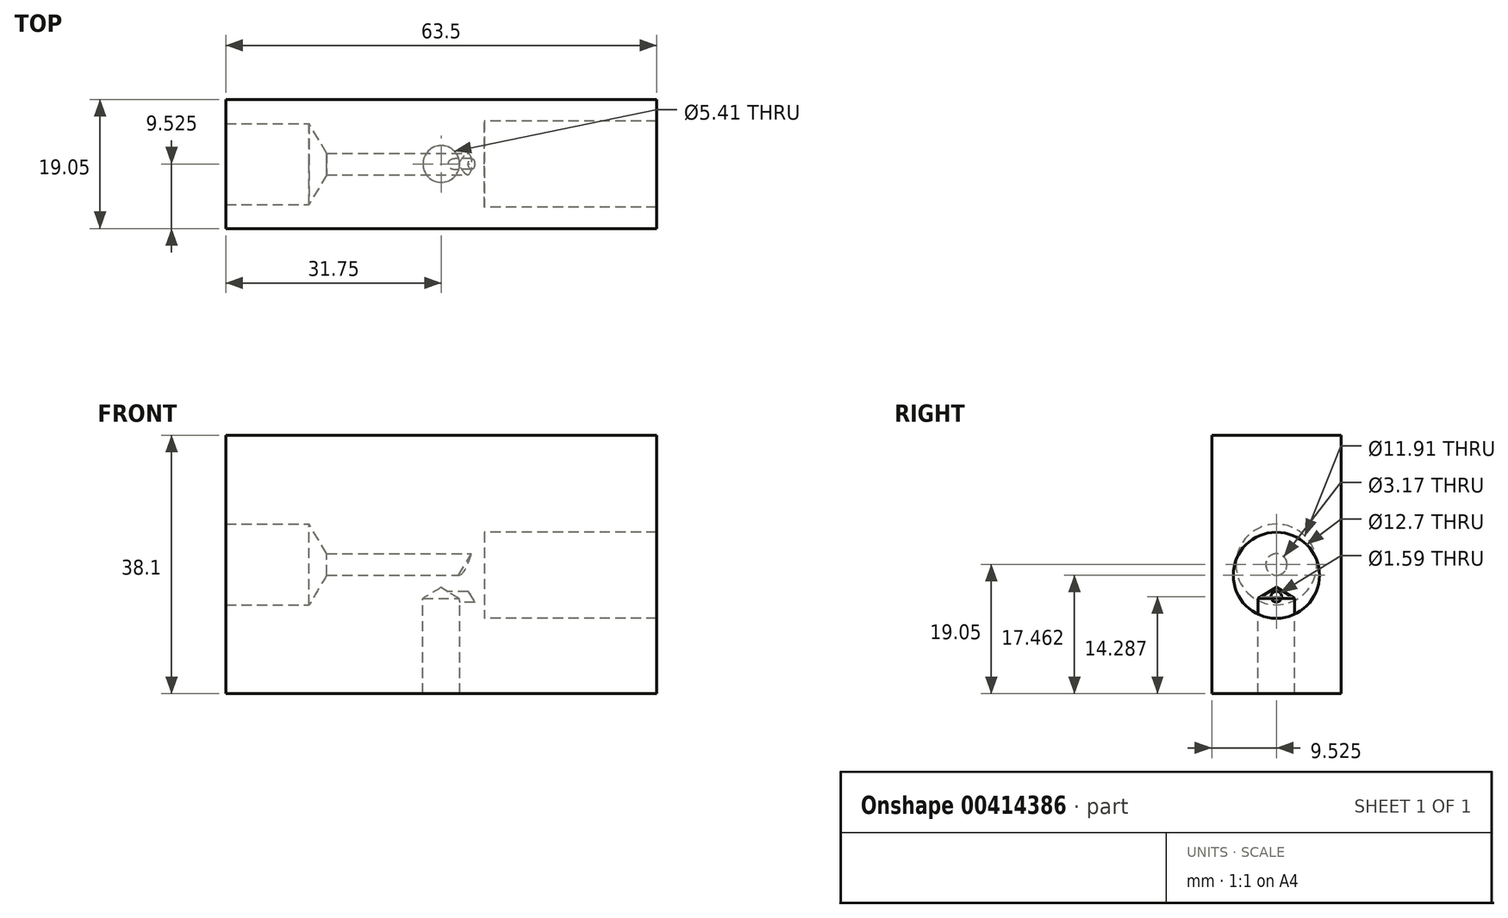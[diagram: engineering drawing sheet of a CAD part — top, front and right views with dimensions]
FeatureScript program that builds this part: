
annotation { "Feature Type Name" : "Feature", "Feature Type Description" : "" }
export const myFeature = defineFeature(function(context is Context, id is Id, definition is map)
    precondition{}
    {
        {
            var Q0;
            Q0=qCreatedBy(makeId("Front.planeOp"),FACE);
            var sketch = newSketch(context, id + "F0", { "sketchPlane" : qUnion([Q0])});
            skLineSegment(sketch, "E0.bottom", {"start": v(0, 0) * mm, "end": v(-63.5, 0) * mm});
            skLineSegment(sketch, "E0.top", {"start": v(0, 38.1) * mm, "end": v(-63.5, 38.1) * mm});
            skLineSegment(sketch, "E0.left", {"start": v(0, 0) * mm, "end": v(0, 38.1) * mm});
            skLineSegment(sketch, "E0.right", {"start": v(-63.5, 0) * mm, "end": v(-63.5, 38.1) * mm});
            skSolve(sketch);
        }
        {
            var Q0;
            Q0=makeQuery(id+"F0.imprint","IMPRINT",FACE,{"disambiguationData":[TD([[makeQuery(id+"F0.imprint","IMPRINT",EDGE,{"derivedFrom":sQuery(id+"F0.wireOp",EDGE,"E0.bottom")}),-1.0]])]});
            extrude(context, id + "F1", {"entities" : qUnion([Q0]), "depth" : 19.05 * mm, "offsetDistance" : 25.4 * mm});
        }
        {
            var Q0;
            Q0=makeQuery(id+"F1.opExtrude","SWEPT_FACE",FACE,{"disambiguationData":[OSD([sQuery(id+"F0.wireOp",EDGE,"E0.right")])]});
            var sketch = newSketch(context, id + "F2", { "sketchPlane" : qUnion([Q0])});
            skPoint(sketch, "E1", {"position": v(9.53, 19.05) * mm});
            skSolve(sketch);
        }
        {
            var Q0;
            Q0=sQuery(id+"F2.wireOp",VERTEX,"E1");
            var Q1;
            Q1=makeQuery(id+"F1.opExtrude","SWEPT_BODY",BODY,{"disambiguationData":[OSD([sQuery(id+"F0.wireOp",EDGE,"E0.bottom"),sQuery(id+"F0.wireOp",EDGE,"E0.top"),sQuery(id+"F0.wireOp",EDGE,"E0.left"),sQuery(id+"F0.wireOp",EDGE,"E0.right")])]});
            hole(context, id + "F3", {"style" : HoleStyle.SIMPLE, "endStyle" : HoleEndStyle.BLIND, "standardTappedOrClearance" : lookupTablePath({ "standard" : "ANSI", "engagement" : "75%", "pitch" : "28 tpi", "size" : "1/2", "type" : "Tapped" }), "standardBlindInLast" : lookupTablePath({ "standard" : "ANSI", "fit" : "Free", "engagement" : "75%", "pitch" : "28 tpi", "size" : "1/2", "type" : "Clearance & tapped" }), "holeDiameter" : 11.9 * mm, "majorDiameter" : 12.7 * mm, "showTappedDepth" : true, "holeDepth" : 12.25 * mm, "tappedDepth" : 9.52 * mm, "tapClearance" : 3, "locations" : qUnion([Q0]), "scope" : qUnion([Q1])});
        }
        {
            var Q0;
            Q0=sQuery(id+"F2.wireOp",VERTEX,"E1");
            var Q1;
            Q1=makeQuery(id+"F1.opExtrude","SWEPT_BODY",BODY,{"disambiguationData":[OSD([sQuery(id+"F0.wireOp",EDGE,"E0.bottom"),sQuery(id+"F0.wireOp",EDGE,"E0.top"),sQuery(id+"F0.wireOp",EDGE,"E0.left"),sQuery(id+"F0.wireOp",EDGE,"E0.right")])]});
            hole(context, id + "F4", {"style" : HoleStyle.SIMPLE, "endStyle" : HoleEndStyle.THROUGH, "holeDiameter" : 3.17 * mm, "majorDiameter" : 12.7 * mm, "tappedDepth" : 9.53 * mm, "tapClearance" : 3, "locations" : qUnion([Q0]), "scope" : qUnion([Q1])});
        }
        {
            var Q0;
            Q0=makeQuery(id+"F1.opExtrude","SWEPT_FACE",FACE,{"disambiguationData":[OSD([sQuery(id+"F0.wireOp",EDGE,"E0.bottom")])]});
            var sketch = newSketch(context, id + "F5", { "sketchPlane" : qUnion([Q0])});
            skPoint(sketch, "E2", {"position": v(-31.75, 9.53) * mm});
            skSolve(sketch);
        }
        {
            var Q0;
            Q0=sQuery(id+"F5.wireOp",VERTEX,"E2");
            var Q1;
            Q1=makeQuery(id+"F1.opExtrude","SWEPT_BODY",BODY,{"disambiguationData":[OSD([sQuery(id+"F0.wireOp",EDGE,"E0.bottom"),sQuery(id+"F0.wireOp",EDGE,"E0.top"),sQuery(id+"F0.wireOp",EDGE,"E0.left"),sQuery(id+"F0.wireOp",EDGE,"E0.right")])]});
            hole(context, id + "F6", {"style" : HoleStyle.SIMPLE, "endStyle" : HoleEndStyle.BLIND, "standardTappedOrClearance" : lookupTablePath({ "standard" : "ANSI", "engagement" : "75%", "pitch" : "28 tpi", "size" : "1/4", "type" : "Tapped" }), "standardBlindInLast" : lookupTablePath({ "standard" : "ANSI", "fit" : "Free", "engagement" : "75%", "pitch" : "28 tpi", "size" : "1/4", "type" : "Clearance & tapped" }), "holeDiameter" : 5.4 * mm, "majorDiameter" : 6.35 * mm, "showTappedDepth" : true, "holeDepth" : 14.06 * mm, "tappedDepth" : 9.52 * mm, "tapClearance" : 5, "locations" : qUnion([Q0]), "scope" : qUnion([Q1])});
        }
        {
            var Q0;
            Q0=makeQuery(id+"F1.opExtrude","SWEPT_FACE",FACE,{"disambiguationData":[OSD([sQuery(id+"F0.wireOp",EDGE,"E0.left")])]});
            var sketch = newSketch(context, id + "F7", { "sketchPlane" : qUnion([Q0])});
            skPoint(sketch, "E3", {"position": v(-9.53, 17.46) * mm});
            skPoint(sketch, "E4", {"position": v(-9.53, 14.29) * mm});
            skSolve(sketch);
        }
        {
            var Q0;
            Q0=sQuery(id+"F7.wireOp",VERTEX,"E3");
            var Q1;
            Q1=makeQuery(id+"F1.opExtrude","SWEPT_BODY",BODY,{"disambiguationData":[OSD([sQuery(id+"F0.wireOp",EDGE,"E0.bottom"),sQuery(id+"F0.wireOp",EDGE,"E0.top"),sQuery(id+"F0.wireOp",EDGE,"E0.left"),sQuery(id+"F0.wireOp",EDGE,"E0.right")])]});
            hole(context, id + "F8", {"style" : HoleStyle.SIMPLE, "endStyle" : HoleEndStyle.BLIND, "holeDiameter" : 12.7 * mm, "majorDiameter" : 6.35 * mm, "holeDepth" : 25.4 * mm, "tappedDepth" : 9.53 * mm, "tapClearance" : 3, "locations" : qUnion([Q0]), "scope" : qUnion([Q1])});
        }
        {
            var Q0;
            Q0=sQuery(id+"F7.wireOp",VERTEX,"E4");
            var Q1;
            Q1=makeQuery(id+"F1.opExtrude","SWEPT_BODY",BODY,{"disambiguationData":[OSD([sQuery(id+"F0.wireOp",EDGE,"E0.bottom"),sQuery(id+"F0.wireOp",EDGE,"E0.top"),sQuery(id+"F0.wireOp",EDGE,"E0.left"),sQuery(id+"F0.wireOp",EDGE,"E0.right")])]});
            hole(context, id + "F9", {"style" : HoleStyle.SIMPLE, "endStyle" : HoleEndStyle.BLIND, "holeDiameter" : 1.59 * mm, "majorDiameter" : 6.35 * mm, "holeDepth" : 3.17 * mm, "tappedDepth" : 9.52 * mm, "tapClearance" : 3, "locations" : qUnion([Q0]), "scope" : qUnion([Q1])});
        }
    });
